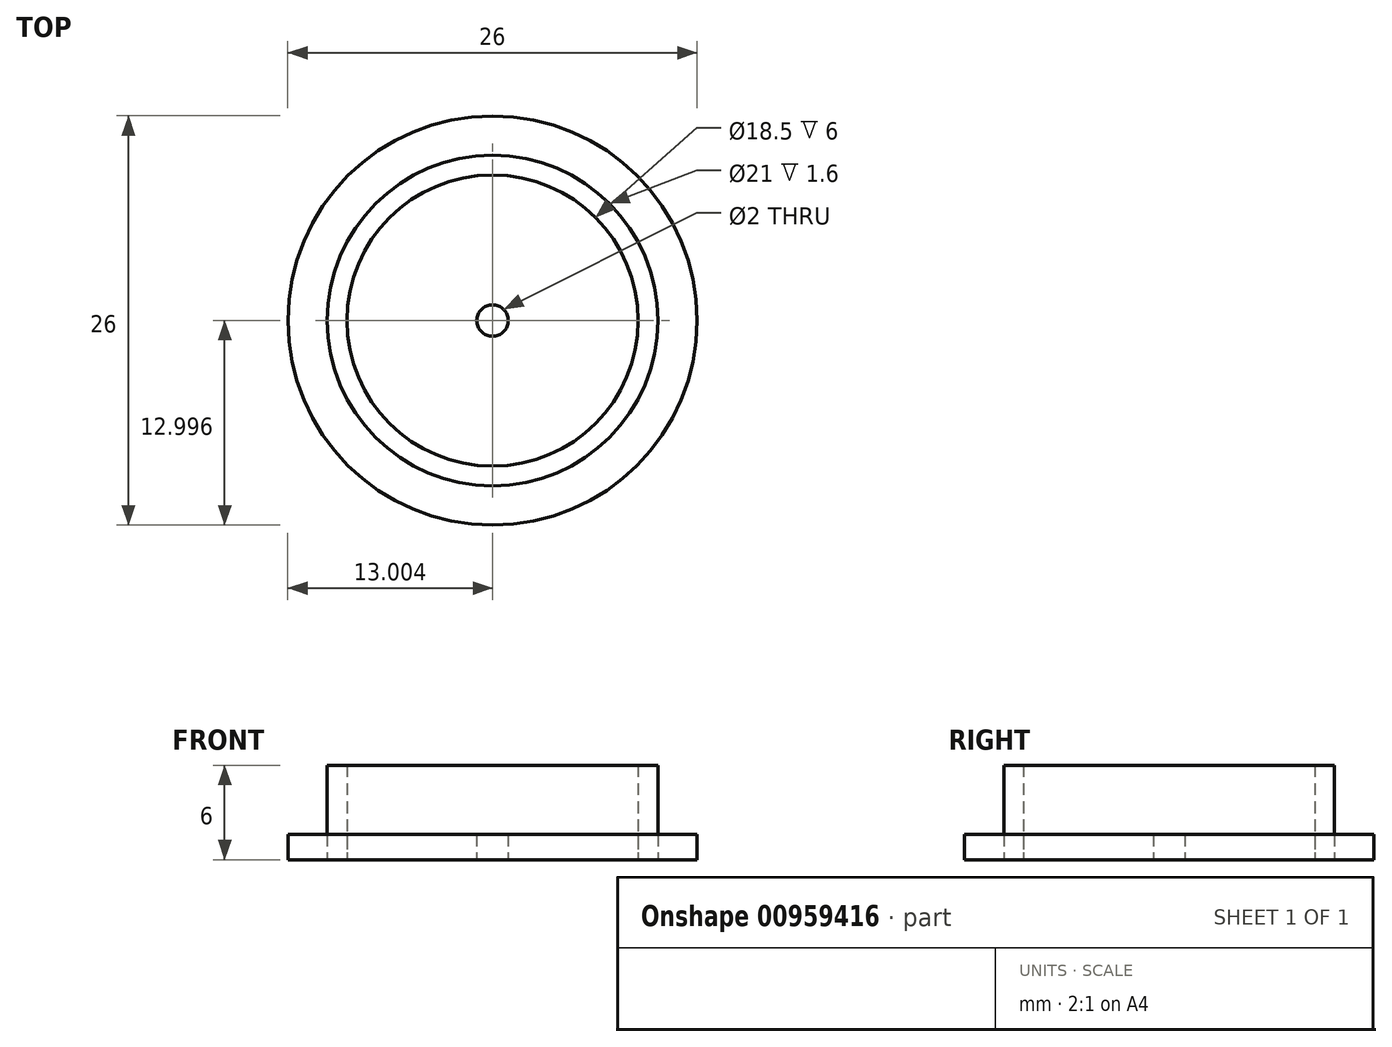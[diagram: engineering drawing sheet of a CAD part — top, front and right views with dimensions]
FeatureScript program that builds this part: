
annotation { "Feature Type Name" : "Feature", "Feature Type Description" : "" }
export const myFeature = defineFeature(function(context is Context, id is Id, definition is map)
    precondition{}
    {
        {
            var Q0;
            Q0=qCreatedBy(makeId("Top.planeOp"),FACE);
            var sketch = newSketch(context, id + "F0", { "sketchPlane" : qUnion([Q0])});
            skCircle(sketch, "E0", {"center": v(-8.6, -9.74) * mm, "radius": 13 * mm});
            skPoint(sketch, "E0.first.point", {"position": v(0, 0) * mm});
            skPoint(sketch, "E0.second.point", {"position": v(-20.72, -14.46) * mm});
            skPoint(sketch, "E0.third.point", {"position": v(2.82, -15.95) * mm});
            skCircle(sketch, "E1", {"center": v(-8.6, -9.74) * mm, "radius": 10.5 * mm});
            skCircle(sketch, "E2", {"center": v(-8.6, -9.74) * mm, "radius": 9.25 * mm});
            skSolve(sketch);
        }
        {
            var Q0;
            Q0=makeQuery(id+"F0.imprint","IMPRINT",FACE,{"disambiguationData":[TD([[makeQuery(id+"F0.imprint","IMPRINT",EDGE,{"derivedFrom":sQuery(id+"F0.wireOp",EDGE,"E0")}),1.0]])]});
            var Q1;
            Q1=makeQuery(id+"F0.imprint","IMPRINT",FACE,{"disambiguationData":[TD([[makeQuery(id+"F0.imprint","IMPRINT",EDGE,{"derivedFrom":sQuery(id+"F0.wireOp",EDGE,"E2")}),1.0]])]});
            extrude(context, id + "F1", {"entities" : qUnion([Q0, Q1]), "depth" : 1.6 * mm, "offsetDistance" : 25 * mm});
        }
        {
            var Q0;
            Q0=makeQuery(id+"F0.imprint","IMPRINT",FACE,{"disambiguationData":[TD([[makeQuery(id+"F0.imprint","IMPRINT",EDGE,{"derivedFrom":sQuery(id+"F0.wireOp",EDGE,"E1")}),1.0]])]});
            extrude(context, id + "F2", {"entities" : qUnion([Q0]), "depth" : 6 * mm, "offsetDistance" : 25 * mm});
        }
        {
            var Q0;
            Q0=sQuery(id+"F0.wireOp",VERTEX,"E0.center");
            var Q1;
            Q1=makeQuery(id+"F1.opExtrude","SWEPT_BODY",BODY,{"disambiguationData":[OSD([sQuery(id+"F0.wireOp",EDGE,"E2")])]});
            hole(context, id + "F3", {"style" : HoleStyle.SIMPLE, "endStyle" : HoleEndStyle.THROUGH, "oppositeDirection" : true, "holeDiameter" : 2 * mm, "majorDiameter" : 5 * mm, "isTappedThrough" : true, "tappedDepth" : 12 * mm, "tapClearance" : 3, "locations" : qUnion([Q0]), "scope" : qUnion([Q1])});
        }
    });
